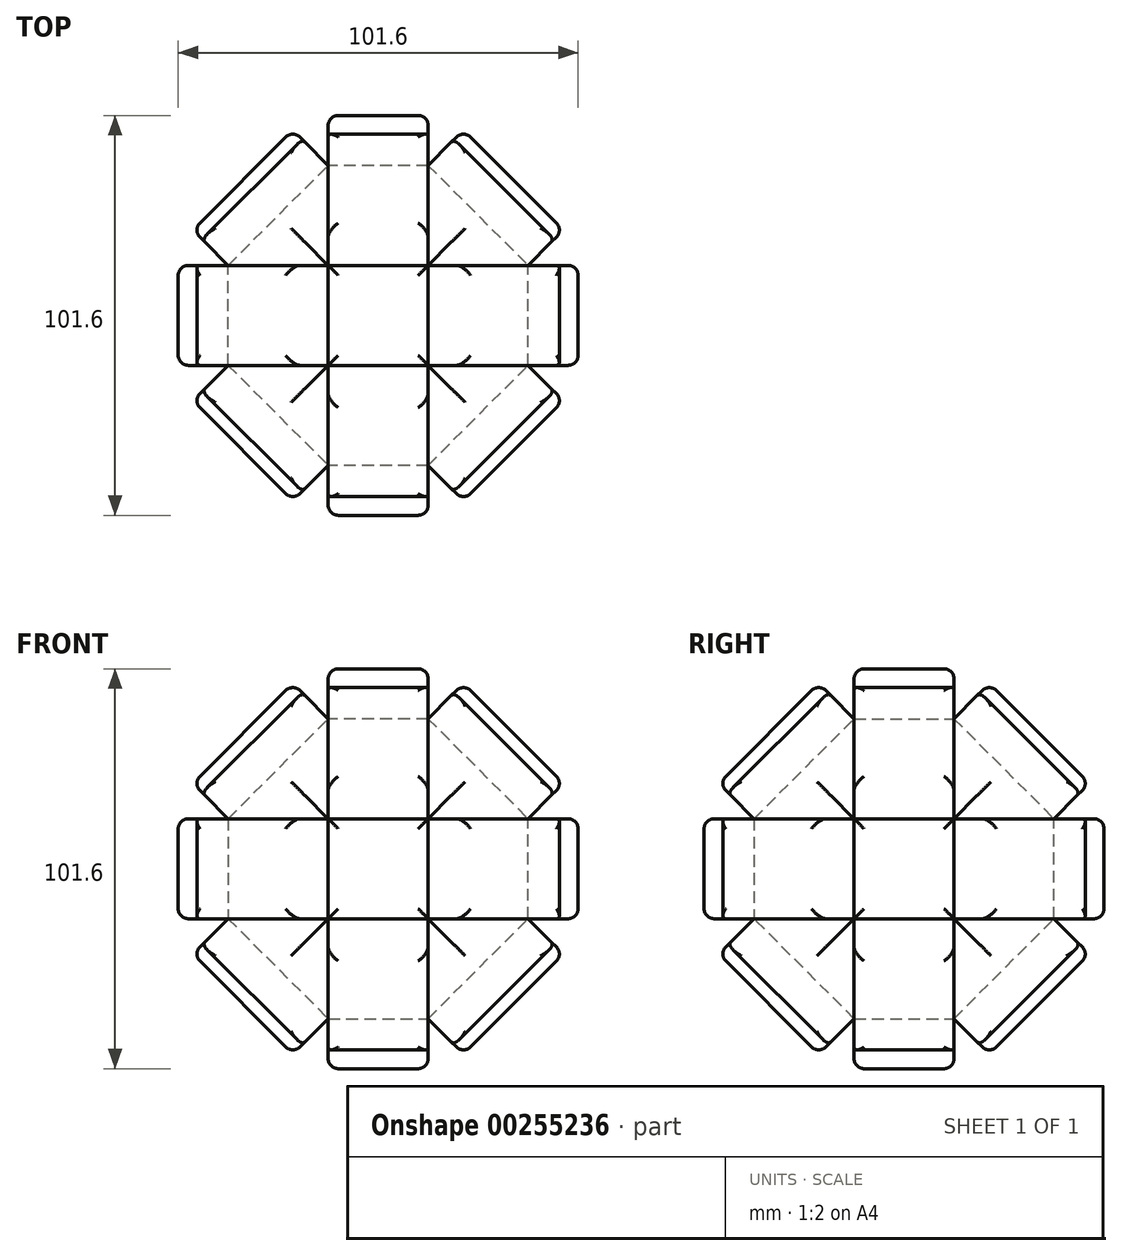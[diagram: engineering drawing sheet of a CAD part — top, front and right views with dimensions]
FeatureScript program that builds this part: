
annotation { "Feature Type Name" : "Feature", "Feature Type Description" : "" }
export const myFeature = defineFeature(function(context is Context, id is Id, definition is map)
    precondition{}
    {
        {
            var Q0;
            Q0=qCreatedBy(makeId("Front.planeOp"),FACE);
            var sketch = newSketch(context, id + "F0", { "sketchPlane" : qUnion([Q0])});
            skLineSegment(sketch, "E0.bottom", {"start": v(38.1, 38.1) * mm, "end": v(-38.1, 38.1) * mm});
            skLineSegment(sketch, "E0.top", {"start": v(38.1, -38.1) * mm, "end": v(-38.1, -38.1) * mm});
            skLineSegment(sketch, "E0.left", {"start": v(38.1, 38.1) * mm, "end": v(38.1, -38.1) * mm});
            skLineSegment(sketch, "E0.right", {"start": v(-38.1, 38.1) * mm, "end": v(-38.1, -38.1) * mm});
            skPoint(sketch, "E0.middle", {"position": v(0, 0) * mm});
            skSolve(sketch);
        }
        {
            var Q0;
            Q0=makeQuery(id+"F0.imprint","IMPRINT",FACE,{"disambiguationData":[TD([[makeQuery(id+"F0.imprint","IMPRINT",EDGE,{"derivedFrom":sQuery(id+"F0.wireOp",EDGE,"E0.bottom")}),1.0]])]});
            extrude(context, id + "F1", {"entities" : qUnion([Q0]), "endBound" : BoundingType.SYMMETRIC, "depth" : 76.2 * mm});
        }
        {
            var Q0;
            Q0=makeQuery(id+"F1.opExtrude","CAP_FACE",FACE,{"disambiguationData":[OSD([sQuery(id+"F0.wireOp",EDGE,"E0.bottom"),sQuery(id+"F0.wireOp",EDGE,"E0.top"),sQuery(id+"F0.wireOp",EDGE,"E0.left"),sQuery(id+"F0.wireOp",EDGE,"E0.right")])],"isStart":false});
            var Q1;
            Q1=makeQuery(id+"F1.opExtrude","SWEPT_FACE",FACE,{"disambiguationData":[OSD([sQuery(id+"F0.wireOp",EDGE,"E0.bottom")])]});
            var Q2;
            Q2=makeQuery(id+"F1.opExtrude","CAP_FACE",FACE,{"disambiguationData":[OSD([sQuery(id+"F0.wireOp",EDGE,"E0.bottom"),sQuery(id+"F0.wireOp",EDGE,"E0.top"),sQuery(id+"F0.wireOp",EDGE,"E0.left"),sQuery(id+"F0.wireOp",EDGE,"E0.right")])],"isStart":true});
            var Q3;
            Q3=makeQuery(id+"F1.opExtrude","SWEPT_FACE",FACE,{"disambiguationData":[OSD([sQuery(id+"F0.wireOp",EDGE,"E0.top")])]});
            chamfer(context, id + "F2", {"entities" : qUnion([Q0, Q1, Q2, Q3]), "width" : 25.4 * mm, "tangentPropagation" : true});
        }
        {
            var Q0;
            Q0=makeQuery(id+"F1.opExtrude","SWEPT_FACE",FACE,{"disambiguationData":[OSD([sQuery(id+"F0.wireOp",EDGE,"E0.top")])]});
            var Q1;
            Q1=makeQuery(id+"F1.opExtrude","SWEPT_FACE",FACE,{"disambiguationData":[OSD([sQuery(id+"F0.wireOp",EDGE,"E0.bottom")])]});
            extrude(context, id + "F3", {"entities" : qUnion([Q0, Q1]), "operationType" : NewBodyOperationType.ADD, "endBound" : BoundingType.SYMMETRIC, "oppositeDirection" : true, "depth" : 25.4 * mm});
        }
        {
            var Q0;
            Q0=makeQuery(id+"F1.opExtrude","SWEPT_FACE",FACE,{"disambiguationData":[OSD([sQuery(id+"F0.wireOp",EDGE,"E0.right")])]});
            var Q1;
            Q1=makeQuery(id+"F1.opExtrude","SWEPT_FACE",FACE,{"disambiguationData":[OSD([sQuery(id+"F0.wireOp",EDGE,"E0.left")])]});
            extrude(context, id + "F4", {"entities" : qUnion([Q0, Q1]), "operationType" : NewBodyOperationType.ADD, "endBound" : BoundingType.SYMMETRIC, "depth" : 25.4 * mm});
        }
        {
            var Q0;
            Q0=makeQuery(id+"F1.opExtrude","CAP_FACE",FACE,{"disambiguationData":[OSD([sQuery(id+"F0.wireOp",EDGE,"E0.bottom"),sQuery(id+"F0.wireOp",EDGE,"E0.top"),sQuery(id+"F0.wireOp",EDGE,"E0.left"),sQuery(id+"F0.wireOp",EDGE,"E0.right")])],"isStart":false});
            var Q1;
            Q1=makeQuery(id+"F1.opExtrude","CAP_FACE",FACE,{"disambiguationData":[OSD([sQuery(id+"F0.wireOp",EDGE,"E0.bottom"),sQuery(id+"F0.wireOp",EDGE,"E0.top"),sQuery(id+"F0.wireOp",EDGE,"E0.left"),sQuery(id+"F0.wireOp",EDGE,"E0.right")])],"isStart":true});
            extrude(context, id + "F5", {"entities" : qUnion([Q0, Q1]), "operationType" : NewBodyOperationType.ADD, "endBound" : BoundingType.SYMMETRIC, "depth" : 25.4 * mm});
        }
        {
            var Q0;
            {var subQ0=sQuery(id+"F0.wireOp",EDGE,"E0.right");var subQ1=sQuery(id+"F0.wireOp",EDGE,"E0.bottom");Q0=makeQuery(id+"F2.opChamfer","BLEND_FACE",FACE,{"disambiguationData":[OSD([subQ1,subQ0]),TDD([makeQuery(id+"F1.opExtrude","CAP_VERTEX",VERTEX,{"disambiguationData":[OSD([subQ1,subQ0])],"isStart":false})])]});}
            var Q1;
            {var subQ0=sQuery(id+"F0.wireOp",EDGE,"E0.left");var subQ1=sQuery(id+"F0.wireOp",EDGE,"E0.top");Q1=makeQuery(id+"F2.opChamfer","BLEND_FACE",FACE,{"disambiguationData":[OSD([subQ1,subQ0]),TDD([makeQuery(id+"F1.opExtrude","CAP_VERTEX",VERTEX,{"disambiguationData":[OSD([subQ1,subQ0])],"isStart":true})])]});}
            extrude(context, id + "F6", {"entities" : qUnion([Q0, Q1]), "operationType" : NewBodyOperationType.ADD, "endBound" : BoundingType.SYMMETRIC, "depth" : 25.4 * mm});
        }
        {
            var Q0;
            {var subQ0=sQuery(id+"F0.wireOp",EDGE,"E0.left");var subQ1=sQuery(id+"F0.wireOp",EDGE,"E0.bottom");Q0=makeQuery(id+"F2.opChamfer","BLEND_FACE",FACE,{"disambiguationData":[OSD([subQ1,subQ0]),TDD([makeQuery(id+"F1.opExtrude","CAP_VERTEX",VERTEX,{"disambiguationData":[OSD([subQ1,subQ0])],"isStart":true})])]});}
            var Q1;
            Q1=makeQuery(id+"F2hY9FCpF3XUTxd_1.opExtrude","CAP_FACE",FACE,{"disambiguationData":[OSD([sQuery(id+"F0.wireOp",EDGE,"E0.top"),sQuery(id+"F0.wireOp",EDGE,"E0.right")])],"isStart":false});
            extrude(context, id + "F7", {"entities" : qUnion([Q0, Q1]), "operationType" : NewBodyOperationType.ADD, "endBound" : BoundingType.SYMMETRIC, "depth" : 25.4 * mm});
        }
        {
            var Q0;
            {var subQ0=sQuery(id+"F0.wireOp",EDGE,"E0.right");var subQ1=sQuery(id+"F0.wireOp",EDGE,"E0.bottom");Q0=makeQuery(id+"F2.opChamfer","BLEND_FACE",FACE,{"disambiguationData":[OSD([subQ1,subQ0]),TDD([makeQuery(id+"F1.opExtrude","CAP_VERTEX",VERTEX,{"disambiguationData":[OSD([subQ1,subQ0])],"isStart":true})])]});}
            var Q1;
            {var subQ0=sQuery(id+"F0.wireOp",EDGE,"E0.left");var subQ1=sQuery(id+"F0.wireOp",EDGE,"E0.top");Q1=makeQuery(id+"F2.opChamfer","BLEND_FACE",FACE,{"disambiguationData":[OSD([subQ1,subQ0]),TDD([makeQuery(id+"F1.opExtrude","CAP_VERTEX",VERTEX,{"disambiguationData":[OSD([subQ1,subQ0])],"isStart":false})])]});}
            extrude(context, id + "F8", {"entities" : qUnion([Q0, Q1]), "operationType" : NewBodyOperationType.ADD, "endBound" : BoundingType.SYMMETRIC, "depth" : 25.4 * mm});
        }
        {
            var Q0;
            {var subQ0=sQuery(id+"F0.wireOp",EDGE,"E0.right");var subQ1=sQuery(id+"F0.wireOp",EDGE,"E0.top");Q0=makeQuery(id+"F2.opChamfer","BLEND_FACE",FACE,{"disambiguationData":[OSD([subQ1,subQ0]),TDD([makeQuery(id+"F1.opExtrude","CAP_VERTEX",VERTEX,{"disambiguationData":[OSD([subQ1,subQ0])],"isStart":false})])]});}
            extrude(context, id + "F9", {"entities" : qUnion([Q0]), "operationType" : NewBodyOperationType.ADD, "endBound" : BoundingType.SYMMETRIC, "depth" : 25.4 * mm});
        }
        {
            var Q0;
            {var subQ0=sQuery(id+"F0.wireOp",EDGE,"E0.right");var subQ1=sQuery(id+"F0.wireOp",EDGE,"E0.top");Q0=makeQuery(id+"F2.opChamfer","BLEND_FACE",FACE,{"disambiguationData":[OSD([subQ1,subQ0]),TDD([makeQuery(id+"F1.opExtrude","CAP_VERTEX",VERTEX,{"disambiguationData":[OSD([subQ1,subQ0])],"isStart":true})])]});}
            var Q1;
            {var subQ0=sQuery(id+"F0.wireOp",EDGE,"E0.left");var subQ1=sQuery(id+"F0.wireOp",EDGE,"E0.bottom");Q1=makeQuery(id+"F2.opChamfer","BLEND_FACE",FACE,{"disambiguationData":[OSD([subQ1,subQ0]),TDD([makeQuery(id+"F1.opExtrude","CAP_VERTEX",VERTEX,{"disambiguationData":[OSD([subQ1,subQ0])],"isStart":false})])]});}
            extrude(context, id + "F10", {"entities" : qUnion([Q0, Q1]), "operationType" : NewBodyOperationType.ADD, "endBound" : BoundingType.SYMMETRIC, "depth" : 25.4 * mm});
        }
        {
            var Q0;
            {var subQ0=sQuery(id+"F0.wireOp",EDGE,"E0.left");var subQ1=sQuery(id+"F0.wireOp",EDGE,"E0.top");Q0=makeQuery(id+"F2.opChamfer","BLEND_FACE",FACE,{"disambiguationData":[OSD([subQ1,subQ0]),TDD([makeQuery(id+"F1.opExtrude","SWEPT_EDGE",EDGE,{"disambiguationData":[OSD([subQ1,subQ0])]})])]});}
            var Q1;
            {var subQ0=sQuery(id+"F0.wireOp",EDGE,"E0.right");var subQ1=sQuery(id+"F0.wireOp",EDGE,"E0.bottom");Q1=makeQuery(id+"F2.opChamfer","BLEND_FACE",FACE,{"disambiguationData":[OSD([subQ1,subQ0]),TDD([makeQuery(id+"F1.opExtrude","SWEPT_EDGE",EDGE,{"disambiguationData":[OSD([subQ1,subQ0])]})])]});}
            extrude(context, id + "F11", {"entities" : qUnion([Q0, Q1]), "operationType" : NewBodyOperationType.ADD, "endBound" : BoundingType.SYMMETRIC, "depth" : 25.4 * mm});
        }
        {
            var Q0;
            {var subQ0=sQuery(id+"F0.wireOp",EDGE,"E0.right");var subQ1=sQuery(id+"F0.wireOp",EDGE,"E0.top");Q0=makeQuery(id+"F2.opChamfer","BLEND_FACE",FACE,{"disambiguationData":[OSD([subQ1,subQ0]),TDD([makeQuery(id+"F1.opExtrude","SWEPT_EDGE",EDGE,{"disambiguationData":[OSD([subQ1,subQ0])]})])]});}
            var Q1;
            {var subQ0=sQuery(id+"F0.wireOp",EDGE,"E0.left");var subQ1=sQuery(id+"F0.wireOp",EDGE,"E0.bottom");Q1=makeQuery(id+"F2.opChamfer","BLEND_FACE",FACE,{"disambiguationData":[OSD([subQ1,subQ0]),TDD([makeQuery(id+"F1.opExtrude","SWEPT_EDGE",EDGE,{"disambiguationData":[OSD([subQ1,subQ0])]})])]});}
            extrude(context, id + "F12", {"entities" : qUnion([Q0, Q1]), "operationType" : NewBodyOperationType.ADD, "endBound" : BoundingType.SYMMETRIC, "depth" : 25.4 * mm});
        }
        {
            var Q0;
            {var subQ0=sQuery(id+"F0.wireOp",EDGE,"E0.left");Q0=makeQuery(id+"F2.opChamfer","BLEND_FACE",FACE,{"disambiguationData":[OSD([subQ0]),TDD([makeQuery(id+"F1.opExtrude","CAP_EDGE",EDGE,{"disambiguationData":[OSD([subQ0])],"isStart":true})])]});}
            var Q1;
            {var subQ0=sQuery(id+"F0.wireOp",EDGE,"E0.right");Q1=makeQuery(id+"F2.opChamfer","BLEND_FACE",FACE,{"disambiguationData":[OSD([subQ0]),TDD([makeQuery(id+"F1.opExtrude","CAP_EDGE",EDGE,{"disambiguationData":[OSD([subQ0])],"isStart":false})])]});}
            extrude(context, id + "F13", {"entities" : qUnion([Q0, Q1]), "operationType" : NewBodyOperationType.ADD, "endBound" : BoundingType.SYMMETRIC, "depth" : 25.4 * mm});
        }
        {
            var Q0;
            {var subQ0=sQuery(id+"F0.wireOp",EDGE,"E0.top");Q0=makeQuery(id+"F2.opChamfer","BLEND_FACE",FACE,{"disambiguationData":[OSD([subQ0]),TDD([makeQuery(id+"F1.opExtrude","CAP_EDGE",EDGE,{"disambiguationData":[OSD([subQ0])],"isStart":true})])]});}
            var Q1;
            {var subQ0=sQuery(id+"F0.wireOp",EDGE,"E0.bottom");Q1=makeQuery(id+"F2.opChamfer","BLEND_FACE",FACE,{"disambiguationData":[OSD([subQ0]),TDD([makeQuery(id+"F1.opExtrude","CAP_EDGE",EDGE,{"disambiguationData":[OSD([subQ0])],"isStart":false})])]});}
            extrude(context, id + "F14", {"entities" : qUnion([Q0, Q1]), "operationType" : NewBodyOperationType.ADD, "endBound" : BoundingType.SYMMETRIC, "depth" : 25.4 * mm});
        }
        {
            var Q0;
            {var subQ0=sQuery(id+"F0.wireOp",EDGE,"E0.top");Q0=makeQuery(id+"F2.opChamfer","BLEND_FACE",FACE,{"disambiguationData":[OSD([subQ0]),TDD([makeQuery(id+"F1.opExtrude","CAP_EDGE",EDGE,{"disambiguationData":[OSD([subQ0])],"isStart":false})])]});}
            var Q1;
            {var subQ0=sQuery(id+"F0.wireOp",EDGE,"E0.bottom");Q1=makeQuery(id+"F2.opChamfer","BLEND_FACE",FACE,{"disambiguationData":[OSD([subQ0]),TDD([makeQuery(id+"F1.opExtrude","CAP_EDGE",EDGE,{"disambiguationData":[OSD([subQ0])],"isStart":true})])]});}
            extrude(context, id + "F15", {"entities" : qUnion([Q0, Q1]), "operationType" : NewBodyOperationType.ADD, "endBound" : BoundingType.SYMMETRIC, "depth" : 25.4 * mm});
        }
        {
            var Q0;
            {var subQ0=sQuery(id+"F0.wireOp",EDGE,"E0.left");Q0=makeQuery(id+"F2.opChamfer","BLEND_FACE",FACE,{"disambiguationData":[OSD([subQ0]),TDD([makeQuery(id+"F1.opExtrude","CAP_EDGE",EDGE,{"disambiguationData":[OSD([subQ0])],"isStart":false})])]});}
            var Q1;
            {var subQ0=sQuery(id+"F0.wireOp",EDGE,"E0.right");Q1=makeQuery(id+"F2.opChamfer","BLEND_FACE",FACE,{"disambiguationData":[OSD([subQ0]),TDD([makeQuery(id+"F1.opExtrude","CAP_EDGE",EDGE,{"disambiguationData":[OSD([subQ0])],"isStart":true})])]});}
            extrude(context, id + "F16", {"entities" : qUnion([Q0, Q1]), "operationType" : NewBodyOperationType.ADD, "endBound" : BoundingType.SYMMETRIC, "depth" : 25.4 * mm});
        }
        {
            var Q0;
            Q0=makeQuery(id+"F4.opExtrude","CAP_FACE",FACE,{"disambiguationData":[OSD([sQuery(id+"F0.wireOp",EDGE,"E0.right")])],"isStart":false});
            var Q1;
            Q1=makeQuery(id+"F12.opExtrude","CAP_FACE",FACE,{"disambiguationData":[OSD([sQuery(id+"F0.wireOp",EDGE,"E0.top"),sQuery(id+"F0.wireOp",EDGE,"E0.right")])],"isStart":false});
            var Q2;
            Q2=makeQuery(id+"F11.opExtrude","CAP_FACE",FACE,{"disambiguationData":[OSD([sQuery(id+"F0.wireOp",EDGE,"E0.top"),sQuery(id+"F0.wireOp",EDGE,"E0.left")])],"isStart":false});
            var Q3;
            Q3=makeQuery(id+"F3.opExtrude","CAP_FACE",FACE,{"disambiguationData":[OSD([sQuery(id+"F0.wireOp",EDGE,"E0.top")])],"isStart":true});
            var Q4;
            Q4=makeQuery(id+"F4.opExtrude","CAP_FACE",FACE,{"disambiguationData":[OSD([sQuery(id+"F0.wireOp",EDGE,"E0.left")])],"isStart":true});
            var Q5;
            Q5=makeQuery(id+"F12.opExtrude","CAP_FACE",FACE,{"disambiguationData":[OSD([sQuery(id+"F0.wireOp",EDGE,"E0.bottom"),sQuery(id+"F0.wireOp",EDGE,"E0.left")])],"isStart":true});
            var Q6;
            Q6=makeQuery(id+"F3.opExtrude","CAP_FACE",FACE,{"disambiguationData":[OSD([sQuery(id+"F0.wireOp",EDGE,"E0.bottom")])],"isStart":false});
            var Q7;
            Q7=makeQuery(id+"F11.opExtrude","CAP_FACE",FACE,{"disambiguationData":[OSD([sQuery(id+"F0.wireOp",EDGE,"E0.bottom"),sQuery(id+"F0.wireOp",EDGE,"E0.right")])],"isStart":true});
            var Q8;
            Q8=makeQuery(id+"F16.opExtrude","CAP_FACE",FACE,{"disambiguationData":[OSD([sQuery(id+"F0.wireOp",EDGE,"E0.right")])],"isStart":true});
            var Q9;
            {var subQ0=sQuery(id+"F0.wireOp",EDGE,"E0.right");var subQ1=sQuery(id+"F0.wireOp",EDGE,"E0.left");var subQ2=sQuery(id+"F0.wireOp",EDGE,"E0.top");var subQ3=sQuery(id+"F0.wireOp",EDGE,"E0.bottom");Q9=makeQuery(id+"F5.opExtrude","CAP_FACE",FACE,{"disambiguationData":[OSD([subQ3,subQ2,subQ1,subQ0]),TDD([makeQuery(id+"F1.opExtrude","CAP_FACE",FACE,{"disambiguationData":[OSD([subQ3,subQ2,subQ1,subQ0])],"isStart":true})])],"isStart":true});}
            var Q10;
            Q10=makeQuery(id+"F13.opExtrude","CAP_FACE",FACE,{"disambiguationData":[OSD([sQuery(id+"F0.wireOp",EDGE,"E0.left")])],"isStart":false});
            var Q11;
            Q11=makeQuery(id+"F16.opExtrude","CAP_FACE",FACE,{"disambiguationData":[OSD([sQuery(id+"F0.wireOp",EDGE,"E0.left")])],"isStart":false});
            var Q12;
            {var subQ0=sQuery(id+"F0.wireOp",EDGE,"E0.right");var subQ1=sQuery(id+"F0.wireOp",EDGE,"E0.left");var subQ2=sQuery(id+"F0.wireOp",EDGE,"E0.top");var subQ3=sQuery(id+"F0.wireOp",EDGE,"E0.bottom");Q12=makeQuery(id+"F5.opExtrude","CAP_FACE",FACE,{"disambiguationData":[OSD([subQ3,subQ2,subQ1,subQ0]),TDD([makeQuery(id+"F1.opExtrude","CAP_FACE",FACE,{"disambiguationData":[OSD([subQ3,subQ2,subQ1,subQ0])],"isStart":false})])],"isStart":false});}
            var Q13;
            Q13=makeQuery(id+"F13.opExtrude","CAP_FACE",FACE,{"disambiguationData":[OSD([sQuery(id+"F0.wireOp",EDGE,"E0.right")])],"isStart":true});
            var Q14;
            Q14=makeQuery(id+"F14.opExtrude","CAP_FACE",FACE,{"disambiguationData":[OSD([sQuery(id+"F0.wireOp",EDGE,"E0.bottom")])],"isStart":true});
            var Q15;
            Q15=makeQuery(id+"F15.opExtrude","CAP_FACE",FACE,{"disambiguationData":[OSD([sQuery(id+"F0.wireOp",EDGE,"E0.top")])],"isStart":false});
            var Q16;
            Q16=makeQuery(id+"F14.opExtrude","CAP_FACE",FACE,{"disambiguationData":[OSD([sQuery(id+"F0.wireOp",EDGE,"E0.top")])],"isStart":false});
            var Q17;
            Q17=makeQuery(id+"F15.opExtrude","CAP_FACE",FACE,{"disambiguationData":[OSD([sQuery(id+"F0.wireOp",EDGE,"E0.bottom")])],"isStart":true});
            var Q18;
            Q18=makeQuery(id+"F10.opExtrude","CAP_FACE",FACE,{"disambiguationData":[OSD([sQuery(id+"F0.wireOp",EDGE,"E0.top"),sQuery(id+"F0.wireOp",EDGE,"E0.right")])],"isStart":false});
            var Q19;
            Q19=makeQuery(id+"F6.opExtrude","CAP_FACE",FACE,{"disambiguationData":[OSD([sQuery(id+"F0.wireOp",EDGE,"E0.top"),sQuery(id+"F0.wireOp",EDGE,"E0.left")])],"isStart":true});
            var Q20;
            Q20=makeQuery(id+"F7.opExtrude","CAP_FACE",FACE,{"disambiguationData":[OSD([sQuery(id+"F0.wireOp",EDGE,"E0.bottom"),sQuery(id+"F0.wireOp",EDGE,"E0.left")])],"isStart":false});
            var Q21;
            Q21=makeQuery(id+"F6.opExtrude","CAP_FACE",FACE,{"disambiguationData":[OSD([sQuery(id+"F0.wireOp",EDGE,"E0.bottom"),sQuery(id+"F0.wireOp",EDGE,"E0.right")])],"isStart":false});
            var Q22;
            Q22=makeQuery(id+"F10.opExtrude","CAP_FACE",FACE,{"disambiguationData":[OSD([sQuery(id+"F0.wireOp",EDGE,"E0.bottom"),sQuery(id+"F0.wireOp",EDGE,"E0.left")])],"isStart":true});
            var Q23;
            {var subQ0=sQuery(id+"F0.wireOp",EDGE,"E0.left");Q23=makeQuery(id+"F2.opChamfer","BLEND_EDGE",EDGE,{"blendedFrom":[makeQuery(id+"F1.opExtrude","CAP_VERTEX",VERTEX,{"disambiguationData":[OSD([sQuery(id+"F0.wireOp",EDGE,"E0.bottom"),subQ0])],"isStart":true}),makeQuery(id+"F1.opExtrude","CAP_EDGE",EDGE,{"disambiguationData":[OSD([subQ0])],"isStart":true})],"blendedInto":[]});}
            var Q24;
            Q24=makeQuery(id+"F9.opExtrude","CAP_FACE",FACE,{"disambiguationData":[OSD([sQuery(id+"F0.wireOp",EDGE,"E0.top"),sQuery(id+"F0.wireOp",EDGE,"E0.right")])],"isStart":false});
            var Q25;
            Q25=makeQuery(id+"F13.opExtrude","CAP_EDGE",EDGE,{"disambiguationData":[OSD([sQuery(id+"F0.wireOp",EDGE,"E0.right")])],"isStart":true});
            var Q26;
            {var subQ0=sQuery(id+"F0.wireOp",EDGE,"E0.right");Q26=makeQuery(id+"F2.opChamfer","BLEND_EDGE",EDGE,{"blendedFrom":[makeQuery(id+"F1.opExtrude","CAP_EDGE",EDGE,{"disambiguationData":[OSD([subQ0])],"isStart":false}),makeQuery(id+"F1.opExtrude","SWEPT_FACE",FACE,{"disambiguationData":[OSD([subQ0])]})],"blendedInto":[makeQuery(id+"F1.opExtrude","SWEPT_FACE",FACE,{"disambiguationData":[OSD([subQ0])]})]});}
            var Q27;
            Q27=makeQuery(id+"F8.opExtrude","CAP_FACE",FACE,{"disambiguationData":[OSD([sQuery(id+"F0.wireOp",EDGE,"E0.top"),sQuery(id+"F0.wireOp",EDGE,"E0.left")])],"isStart":true});
            var Q28;
            Q28=makeQuery(id+"F8.opExtrude","CAP_FACE",FACE,{"disambiguationData":[OSD([sQuery(id+"F0.wireOp",EDGE,"E0.bottom"),sQuery(id+"F0.wireOp",EDGE,"E0.right")])],"isStart":false});
            fillet(context, id + "F17", {"entities" : qUnion([Q0, Q1, Q2, Q3, Q4, Q5, Q6, Q7, Q8, Q9, Q10, Q11, Q12, Q13, Q14, Q15, Q16, Q17, Q18, Q19, Q20, Q21, Q22, Q23, Q24, Q25, Q26, Q27, Q28]), "radius" : 2.54 * mm, "tangentPropagation" : true, "allowEdgeOverflow" : false});
        }
    });
